# Revit family: Deca_Acabamento para Registro de Pressão_Polo_4916.C33.PQ
name_source: partatom
category: Plumbing Fixtures
revit_build: Autodesk Revit Architecture 2012 (Build: 20110309_2315(x64)
units: mm (PartAtom-declared; Revit-internal decimal feet)

## types (9) — shared parameters
Acompanha o Produto = Não Aplicável
Aprovado por = Contino/quattroD
Atendimento ao Cliente = 0800-011-7073
Criador por = Contino/quattroD
Código = 4916.C33.PQ
Description = Acabamento para registro de pressão
Descrição = Acabamento para registro de pressão
Fabricante = Deca
Flow Pressure = 0.00 psi
Informações Complementares = Acompanha mecanismo de 1/2 volta - MVR II (4688.005)
Linha = Polo
Louça/Metais = Metais
Manufacturer = Deca
Material = Metal
Model = 4916.C33.PQ
Peso Liquido (Kg) = 0.524
Pressão = 2 a 40 mca
Produto = Acabamento para registro de pressão linha Polo
Registro = Deca CR10 Cromado Metal
Segmento = Medio
URL = www.deca.com.br
Vendido Separadamente = Não Aplicável
zero-valued in all types: CWFU, Default Elevation

## per-type parameters (varying)
| type | Base de Registro_Family | Diâmetro Ponto de Agua | Max. | Raio Ponto de Agua |
| 4416.102 - DN 15 (1/2") - 4916.C33.PQ | Deca_Base de Registro de Pressão_4416 : 4416.102 - DN 15 (1/2") | 15 mm  [stored 0.0492126 ft] | 45 mm  [stored 0.147638 ft] | 8 mm  [stored 0.0262467 ft] |
| 4416.202 - DN 20 (3/4") - 4916.C33.PQ | Deca_Base de Registro de Pressão_4416 : 4416.202 - DN 20 (3/4") | 20 mm  [stored 0.0656168 ft] | 40 mm  [stored 0.131234 ft] | 10 mm  [stored 0.0328084 ft] |
| Base Fácil PVC 20mm (4416.102.PVC) | Deca_Base de Registro de Pressão_4416 : 4416.202 - DN 20 (3/4") | 20 mm  [stored 0.0656168 ft] | 40 mm  [stored 0.131234 ft] | 10 mm  [stored 0.0328084 ft] |
| Base Fácil PVC 25mm (4416.202.PVC) | Deca_Base de Registro de Pressão_4416 : 4416.202 - DN 20 (3/4") | 25 mm  [stored 0.082021 ft] | 40 mm  [stored 0.131234 ft] | 13 mm |
| Base Fácil PPR 20mm (4416.102.PPR) | Deca_Base de Registro de Pressão_4416 : 4416.202 - DN 20 (3/4") | 20 mm  [stored 0.0656168 ft] | 40 mm  [stored 0.131234 ft] | 10 mm  [stored 0.0328084 ft] |
| Base Fácil PPR 25mm (4416.202.PPR) | Deca_Base de Registro de Pressão_4416 : 4416.202 - DN 20 (3/4") | 25 mm  [stored 0.082021 ft] | 40 mm  [stored 0.131234 ft] | 13 mm |
| Base Fácil CPVC 15mm (4416.102.CPVC) | Deca_Base de Registro de Pressão_4416 : 4416.202 - DN 20 (3/4") | 15 mm  [stored 0.0492126 ft] | 40 mm  [stored 0.131234 ft] | 8 mm  [stored 0.0262467 ft] |
| Base Fácil CPVC 22mm (4416.202.CPVC) | Deca_Base de Registro de Pressão_4416 : 4416.202 - DN 20 (3/4") | 22 mm  [stored 0.0721785 ft] | 40 mm  [stored 0.131234 ft] | 11 mm  [stored 0.0360892 ft] |
| Base Fácil CPVC 28mm (4416.302.CPVC) | Deca_Base de Registro de Pressão_4416 : 4416.202 - DN 20 (3/4") | 28 mm  [stored 0.0918635 ft] | 40 mm  [stored 0.131234 ft] | 14 mm  [stored 0.0459318 ft] |

note: [stored X ft] marks values corroborated as IEEE doubles in the binary element streams (Revit-internal decimal feet)

## geometry (parser evidence)
native form markers: Blend x2, Sweep x6
no freeform markers — native parametric forms only
